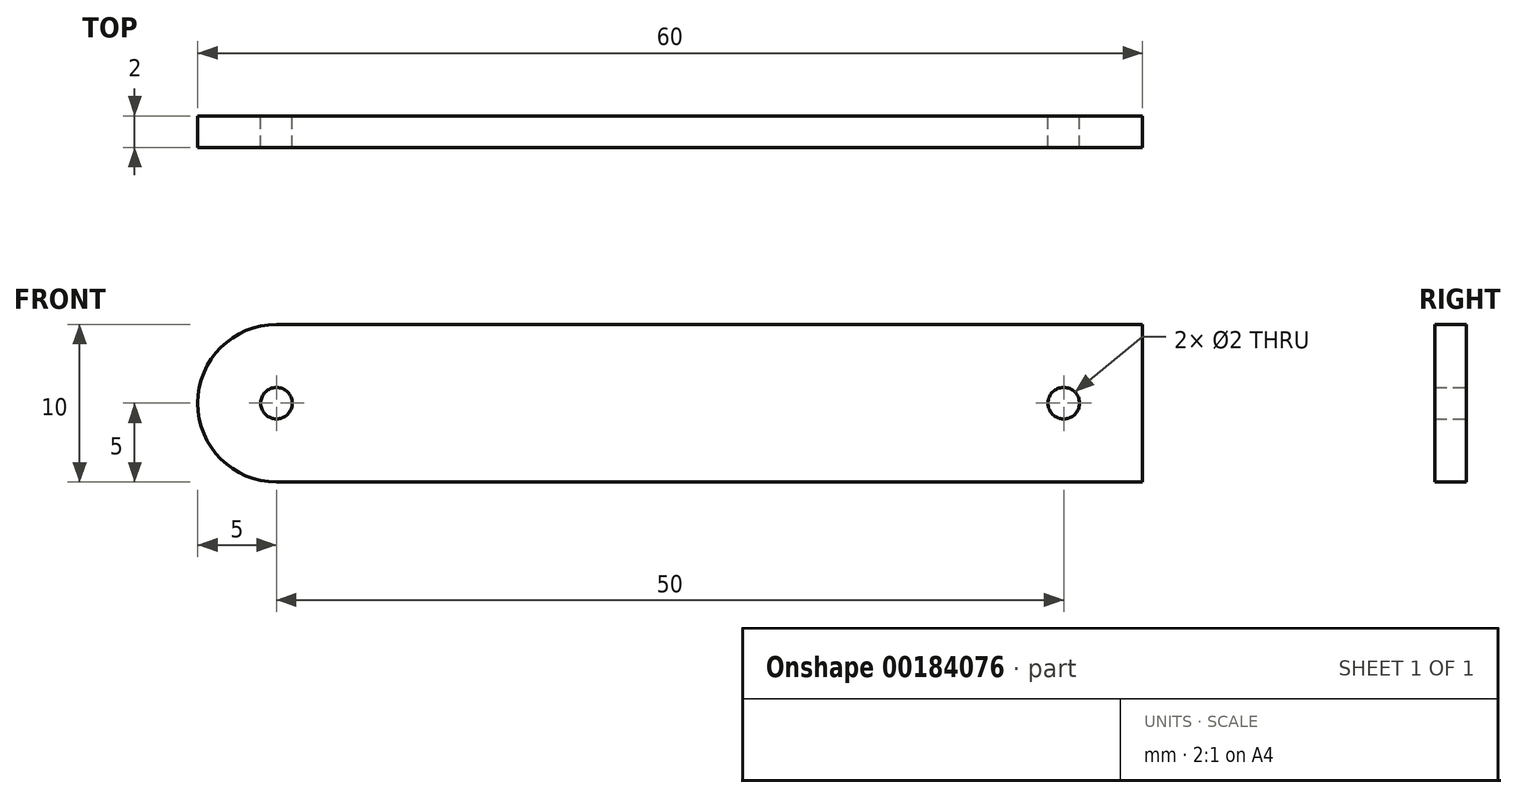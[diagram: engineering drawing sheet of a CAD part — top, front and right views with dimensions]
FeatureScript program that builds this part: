
annotation { "Feature Type Name" : "Feature", "Feature Type Description" : "" }
export const myFeature = defineFeature(function(context is Context, id is Id, definition is map)
    precondition{}
    {
        {
            var Q0;
            Q0=qCreatedBy(makeId("Front.planeOp"),FACE);
            var sketch = newSketch(context, id + "F0", { "sketchPlane" : qUnion([Q0])});
            skLineSegment(sketch, "E0.bottom", {"start": v(0, 0) * mm, "end": v(55, 0) * mm});
            skLineSegment(sketch, "E0.top", {"start": v(0, -10) * mm, "end": v(55, -10) * mm});
            skLineSegment(sketch, "E0.right", {"start": v(55, 0) * mm, "end": v(55, -10) * mm});
            skArc(sketch, "E1", {"start": v(0, 0) * mm, "mid": v(-5, -5) * mm, "end": v(0, -10) * mm});
            skCircle(sketch, "E2", {"center": v(0, -5) * mm, "radius": 1 * mm});
            skCircle(sketch, "E3", {"center": v(50, -5) * mm, "radius": 1 * mm});
            skPoint(sketch, "E3.centerSnap0", {"position": v(-5, -5) * mm});
            skSolve(sketch);
        }
        {
            var Q0;
            Q0 = qSketchRegion(id + "F0", true);
            extrude(context, id + "F1", {"entities" : qUnion([Q0]), "depth" : 2 * mm});
        }
    });
